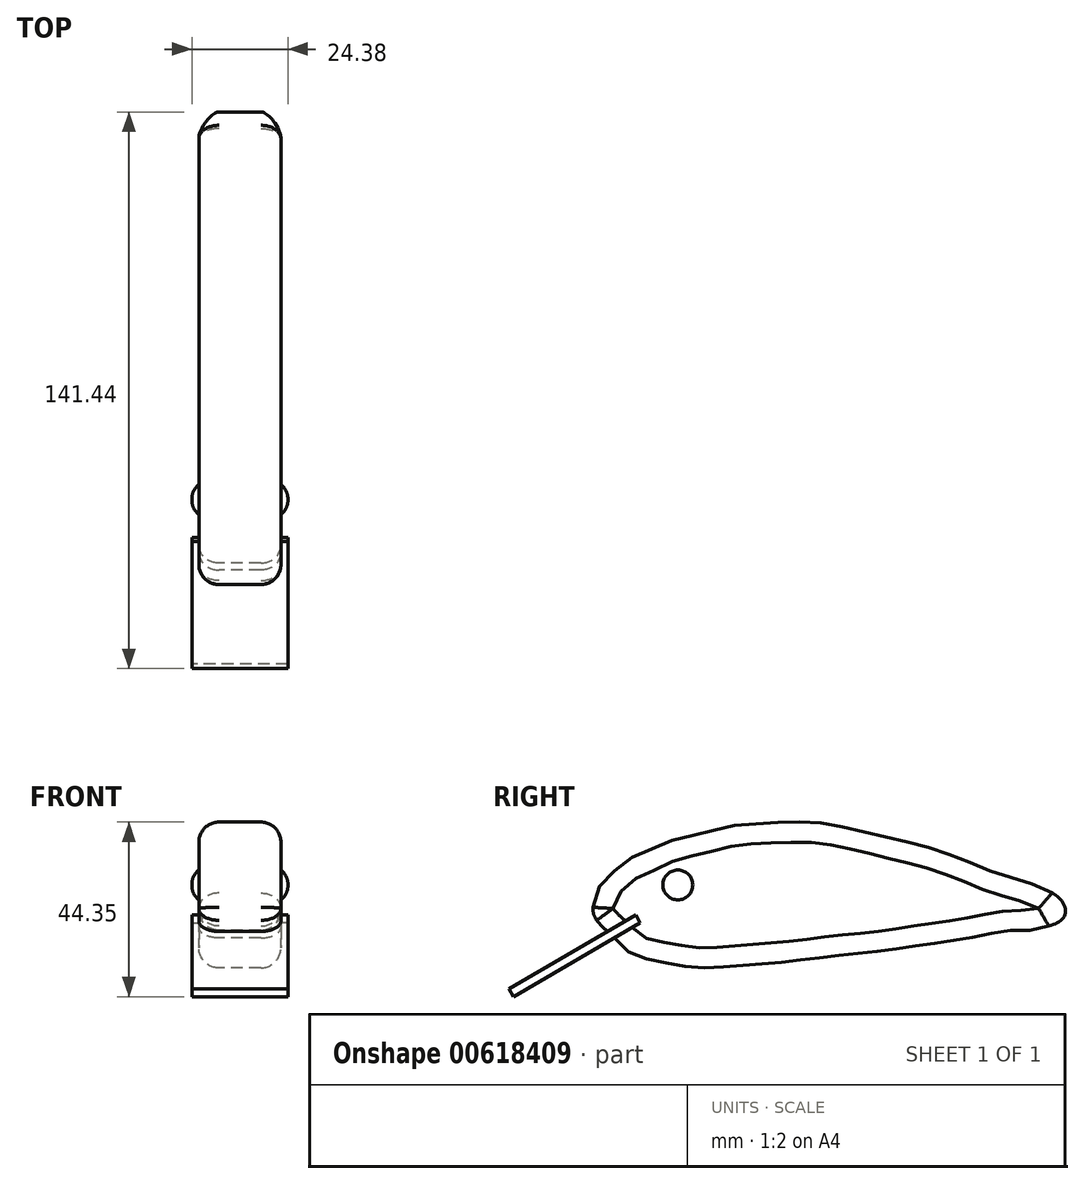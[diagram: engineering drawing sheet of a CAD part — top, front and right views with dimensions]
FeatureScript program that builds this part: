
annotation { "Feature Type Name" : "Feature", "Feature Type Description" : "" }
export const myFeature = defineFeature(function(context is Context, id is Id, definition is map)
    precondition{}
    {
        {
            var Q0;
            Q0=qCreatedBy(makeId("Right.planeOp"),FACE);
            var sketch = newSketch(context, id + "F0", { "sketchPlane" : qUnion([Q0])});
            skFitSpline(sketch, "E0", {"points": [v(-51.98, 0) * mm, v(-48.03, 3.84) * mm, v(-45, 6.4) * mm, v(-40.12, 8.49) * mm, v(-34.77, 11.05) * mm, v(-26.86, 12.9) * mm, v(-20.82, 14.54) * mm, v(-13.84, 15.47) * mm, v(-3.14, 15.93) * mm, v(4.3, 15.7) * mm, v(10.35, 14.54) * mm, v(16.63, 13.14) * mm, v(26.17, 10.82) * mm, v(30.82, 9.65) * mm, v(37.1, 7.56) * mm, v(43.14, 5.23) * mm, v(48.26, 3.14) * mm, v(58.5, 0) * mm, v(62.68, -1.98) * mm, v(65.24, -4.07) * mm, v(66.17, -7.1) * mm, v(64.78, -9.19) * mm, v(61.52, -10.58) * mm, v(57.33, -11.51) * mm, v(53.15, -11.51) * mm, v(46.87, -12.44) * mm, v(36.63, -14.3) * mm, v(26.86, -15.7) * mm, v(17.1, -17.1) * mm, v(9.65, -17.8) * mm, v(0, -18.96) * mm, v(-8.95, -19.89) * mm, v(-18.26, -20.58) * mm, v(-27.1, -21.05) * mm, v(-35, -19.89) * mm, v(-40.59, -18.72) * mm, v(-45, -16.86) * mm, v(-47.8, -14.07) * mm, v(-52.91, -8.95) * mm, v(-53.84, -5.47) * mm, v(-51.98, 0) * mm]});
            skSolve(sketch);
        }
        {
            var Q0;
            Q0=makeQuery(id+"F0.imprint","IMPRINT",FACE,{"disambiguationData":[TD([[makeQuery(id+"F0.imprint","IMPRINT",EDGE,{"derivedFrom":sQuery(id+"F0.wireOp",EDGE,"E0")}),-1.0]])]});
            extrude(context, id + "F1", {"entities" : qUnion([Q0]), "depth" : 10.4 * mm, "offsetDistance" : 25.4 * mm});
        }
        {
            var Q0;
            Q0=qCreatedBy(makeId("Right.planeOp"),FACE);
            var sketch = newSketch(context, id + "F2", { "sketchPlane" : qUnion([Q0])});
            skLineSegment(sketch, "E1", {"start": v(-42.91, -7.56) * mm, "end": v(-75.24, -26.4) * mm});
            skLineSegment(sketch, "E2", {"start": v(-75.24, -26.4) * mm, "end": v(-74.08, -28.4) * mm});
            skLineSegment(sketch, "E3", {"start": v(-74.08, -28.4) * mm, "end": v(-41.92, -9.66) * mm});
            skLineSegment(sketch, "E4", {"start": v(-41.92, -9.66) * mm, "end": v(-42.91, -7.56) * mm});
            skSolve(sketch);
        }
        {
            var Q0;
            Q0=makeQuery(id+"F2.imprint","IMPRINT",FACE,{"disambiguationData":[TD([[makeQuery(id+"F2.imprint","IMPRINT",EDGE,{"derivedFrom":sQuery(id+"F2.wireOp",EDGE,"E1")}),1.0]])]});
            extrude(context, id + "F3", {"entities" : qUnion([Q0]), "operationType" : NewBodyOperationType.ADD, "depth" : 12.2 * mm, "offsetDistance" : 25.4 * mm});
        }
        {
            var Q0;
            Q0=makeQuery(id+"F1.opExtrude","CAP_EDGE",EDGE,{"disambiguationData":[OSD([sQuery(id+"F0.wireOp",EDGE,"E0")])],"isStart":false});
            fillet(context, id + "F4", {"entities" : qUnion([Q0]), "radius" : 5.08 * mm, "tangentPropagation" : true, "allowEdgeOverflow" : false});
        }
        {
            var Q0;
            Q0=qCreatedBy(makeId("Right.planeOp"),FACE);
            var sketch = newSketch(context, id + "F5", { "sketchPlane" : qUnion([Q0])});
            skCircle(sketch, "E5", {"center": v(-32.29, 0) * mm, "radius": 3.8 * mm});
            skSolve(sketch);
        }
        {
            var Q0;
            Q0 = qSketchRegion(id + "F5", true);
            extrude(context, id + "F6", {"entities" : qUnion([Q0]), "operationType" : NewBodyOperationType.ADD, "depth" : 12.2 * mm, "offsetDistance" : 25.4 * mm});
        }
        {
            var Q0;
            Q0=makeQuery(id+"F6.opExtrude","CAP_EDGE",EDGE,{"disambiguationData":[OSD([sQuery(id+"F5.wireOp",EDGE,"E5")])],"isStart":false});
            fillet(context, id + "F7", {"entities" : qUnion([Q0]), "radius" : 4.48 * mm, "tangentPropagation" : true, "allowEdgeOverflow" : false});
        }
        {
            var Q0;
            Q0=makeQuery(id+"F1.opExtrude","SWEPT_BODY",BODY,{"disambiguationData":[OSD([sQuery(id+"F0.wireOp",EDGE,"E0")])]});
            var Q1;
            Q1=qCreatedBy(makeId("Right.planeOp"),FACE);
            mirror(context, id + "F8", {"operationType" : NewBodyOperationType.ADD, "entities" : qUnion([Q0]), "mirrorPlane" : qUnion([Q1])});
        }
    });
